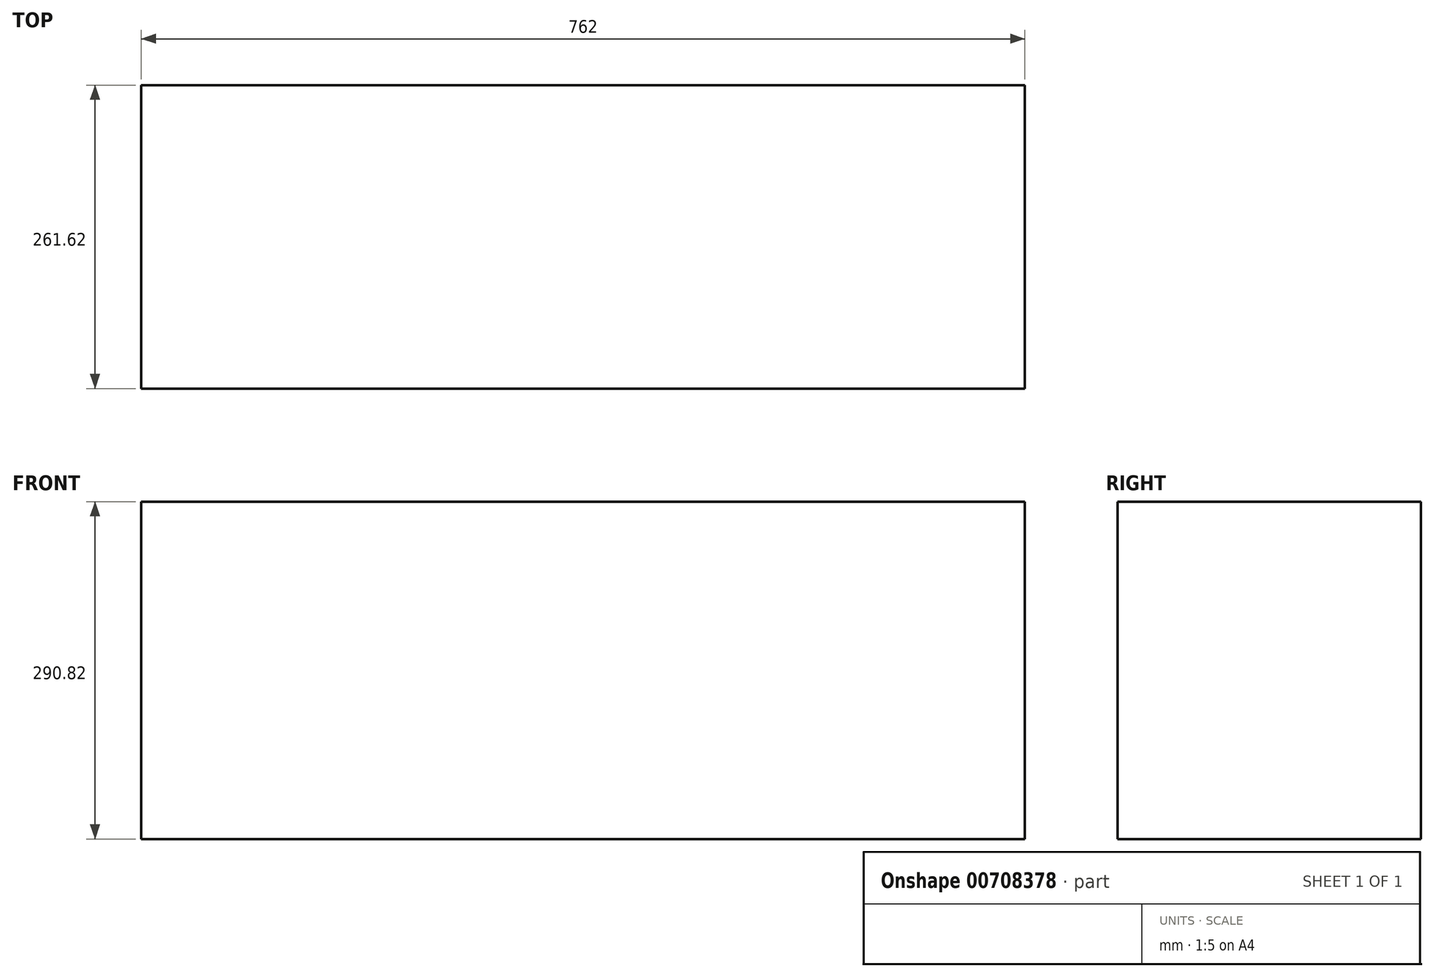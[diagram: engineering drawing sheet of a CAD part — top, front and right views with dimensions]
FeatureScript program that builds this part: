
annotation { "Feature Type Name" : "Feature", "Feature Type Description" : "" }
export const myFeature = defineFeature(function(context is Context, id is Id, definition is map)
    precondition{}
    {
        {
            var Q0;
            Q0=qCreatedBy(makeId("Front.planeOp"),FACE);
            var sketch = newSketch(context, id + "F0", { "sketchPlane" : qUnion([Q0])});
            skLineSegment(sketch, "E0.bottom", {"start": v(-381, 139.68) * mm, "end": v(381, 139.68) * mm});
            skLineSegment(sketch, "E0.top", {"start": v(-381, -151.14) * mm, "end": v(381, -151.14) * mm});
            skLineSegment(sketch, "E0.left", {"start": v(-381, 139.68) * mm, "end": v(-381, -151.14) * mm});
            skLineSegment(sketch, "E0.right", {"start": v(381, 139.68) * mm, "end": v(381, -151.14) * mm});
            skSolve(sketch);
        }
        {
            var Q0;
            Q0=makeQuery(id+"F0.imprint","IMPRINT",FACE,{"disambiguationData":[TD([[makeQuery(id+"F0.imprint","IMPRINT",EDGE,{"derivedFrom":sQuery(id+"F0.wireOp",EDGE,"E0.bottom")}),-1.0]])]});
            extrude(context, id + "F1", {"entities" : qUnion([Q0]), "depth" : 261.62 * mm, "offsetDistance" : 25.4 * mm});
        }
    });
